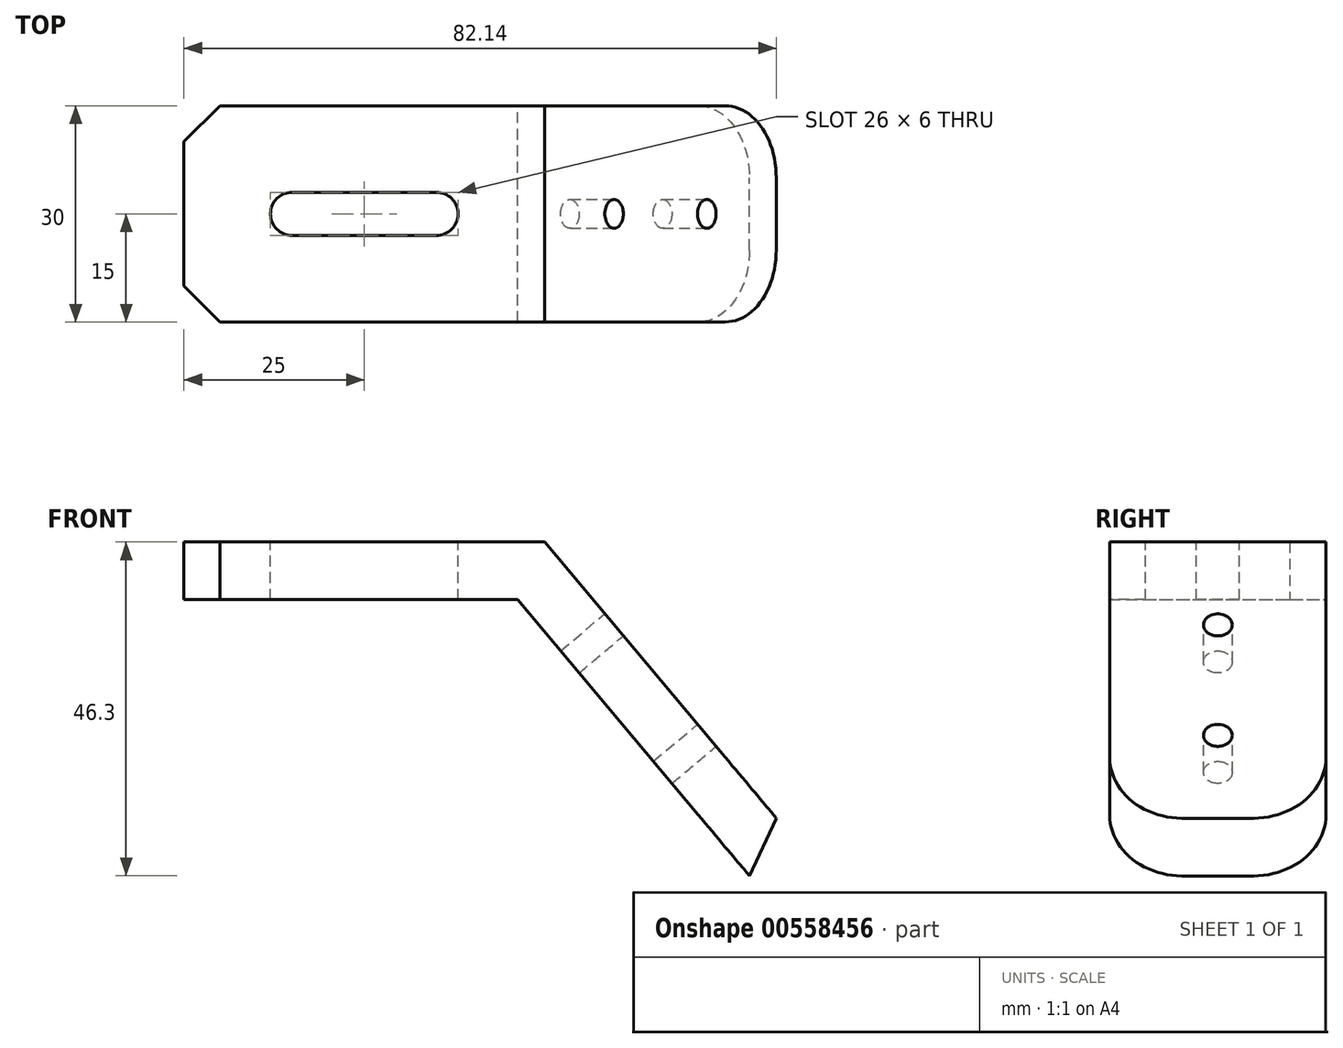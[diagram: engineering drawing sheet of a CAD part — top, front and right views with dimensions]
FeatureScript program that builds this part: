
annotation { "Feature Type Name" : "Feature", "Feature Type Description" : "" }
export const myFeature = defineFeature(function(context is Context, id is Id, definition is map)
    precondition{}
    {
        {
            var Q0;
            Q0=qCreatedBy(makeId("Front.planeOp"),FACE);
            var sketch = newSketch(context, id + "F0", { "sketchPlane" : qUnion([Q0])});
            skLineSegment(sketch, "E0", {"start": v(0, 0) * mm, "end": v(46.27, 0) * mm});
            skLineSegment(sketch, "E1", {"start": v(78.4, -38.3) * mm, "end": v(46.27, 0) * mm});
            skLineSegment(sketch, "E2.0", {"start": v(82.14, -30.3) * mm, "end": v(50, 8) * mm});
            skLineSegment(sketch, "E2.1", {"start": v(0, 8) * mm, "end": v(50, 8) * mm});
            skLineSegment(sketch, "E3", {"start": v(0, 0) * mm, "end": v(0, 8) * mm});
            skLineSegment(sketch, "E4", {"start": v(78.4, -38.3) * mm, "end": v(82.14, -30.3) * mm});
            skSolve(sketch);
        }
        {
            var Q0;
            Q0 = qSketchRegion(id + "F0", true);
            extrude(context, id + "F1", {"entities" : qUnion([Q0]), "endBound" : BoundingType.SYMMETRIC, "depth" : 30 * mm, "offsetDistance" : 25 * mm});
        }
        {
            var Q0;
            Q0=makeQuery(id+"F1.opExtrude","SWEPT_FACE",FACE,{"disambiguationData":[OSD([sQuery(id+"F0.wireOp",EDGE,"E2.1")])]});
            var sketch = newSketch(context, id + "F2", { "sketchPlane" : qUnion([Q0])});
            skLineSegment(sketch, "E5", {"start": v(15, 0) * mm, "end": v(35, 0) * mm});
            skArc(sketch, "E6.0.startCap", {"start": v(15, -3) * mm, "mid": v(12, 0) * mm, "end": v(15, 3) * mm});
            skArc(sketch, "E6.0.endCap", {"start": v(35, 3) * mm, "mid": v(38, 0) * mm, "end": v(35, -3) * mm});
            skLineSegment(sketch, "E6.0.left", {"start": v(15, 3) * mm, "end": v(35, 3) * mm});
            skLineSegment(sketch, "E6.0.right", {"start": v(15, -3) * mm, "end": v(35, -3) * mm});
            skSolve(sketch);
        }
        {
            var Q0;
            Q0 = qSketchRegion(id + "F2", true);
            extrude(context, id + "F3", {"entities" : qUnion([Q0]), "operationType" : NewBodyOperationType.REMOVE, "endBound" : BoundingType.THROUGH_ALL, "oppositeDirection" : true, "depth" : 25 * mm, "offsetDistance" : 25 * mm});
        }
        {
            var Q0;
            Q0=makeQuery(id+"F1.opExtrude","SWEPT_FACE",FACE,{"disambiguationData":[OSD([sQuery(id+"F0.wireOp",EDGE,"E2.0")])]});
            var sketch = newSketch(context, id + "F4", { "sketchPlane" : qUnion([Q0])});
            skPoint(sketch, "E7", {"position": v(0, -41.01) * mm});
            skPoint(sketch, "E8", {"position": v(0, -61.01) * mm});
            skSolve(sketch);
        }
        {
            var Q0;
            Q0=sQuery(id+"F4.wireOp",VERTEX,"E7");
            var Q1;
            Q1=sQuery(id+"F4.wireOp",VERTEX,"E8");
            var Q2;
            Q2=makeQuery(id+"F1.opExtrude","SWEPT_BODY",BODY,{"disambiguationData":[OSD([sQuery(id+"F0.wireOp",EDGE,"E0"),sQuery(id+"F0.wireOp",EDGE,"E1"),sQuery(id+"F0.wireOp",EDGE,"E2.0"),sQuery(id+"F0.wireOp",EDGE,"E2.1"),sQuery(id+"F0.wireOp",EDGE,"E3"),sQuery(id+"F0.wireOp",EDGE,"E4")])]});
            hole(context, id + "F5", {"style" : HoleStyle.SIMPLE, "endStyle" : HoleEndStyle.THROUGH, "holeDiameter" : 4 * mm, "isTappedThrough" : true, "tappedDepth" : 12 * mm, "tapClearance" : 3, "locations" : qUnion([Q0, Q1]), "scope" : qUnion([Q2])});
        }
        {
            var Q0;
            Q0=makeQuery(id+"F1.opExtrude","CAP_EDGE",EDGE,{"disambiguationData":[OSD([sQuery(id+"F0.wireOp",EDGE,"E4")])],"isStart":false});
            var Q1;
            Q1=makeQuery(id+"F1.opExtrude","CAP_EDGE",EDGE,{"disambiguationData":[OSD([sQuery(id+"F0.wireOp",EDGE,"E4")])],"isStart":true});
            fillet(context, id + "F6", {"entities" : qUnion([Q0, Q1]), "radius" : 10 * mm, "tangentPropagation" : true, "allowEdgeOverflow" : false});
        }
        {
            var Q0;
            Q0=makeQuery(id+"F1.opExtrude","CAP_EDGE",EDGE,{"disambiguationData":[OSD([sQuery(id+"F0.wireOp",EDGE,"E3")])],"isStart":true});
            var Q1;
            Q1=makeQuery(id+"F1.opExtrude","CAP_EDGE",EDGE,{"disambiguationData":[OSD([sQuery(id+"F0.wireOp",EDGE,"E3")])],"isStart":false});
            chamfer(context, id + "F7", {"entities" : qUnion([Q0, Q1]), "width" : 5 * mm, "tangentPropagation" : true});
        }
    });
